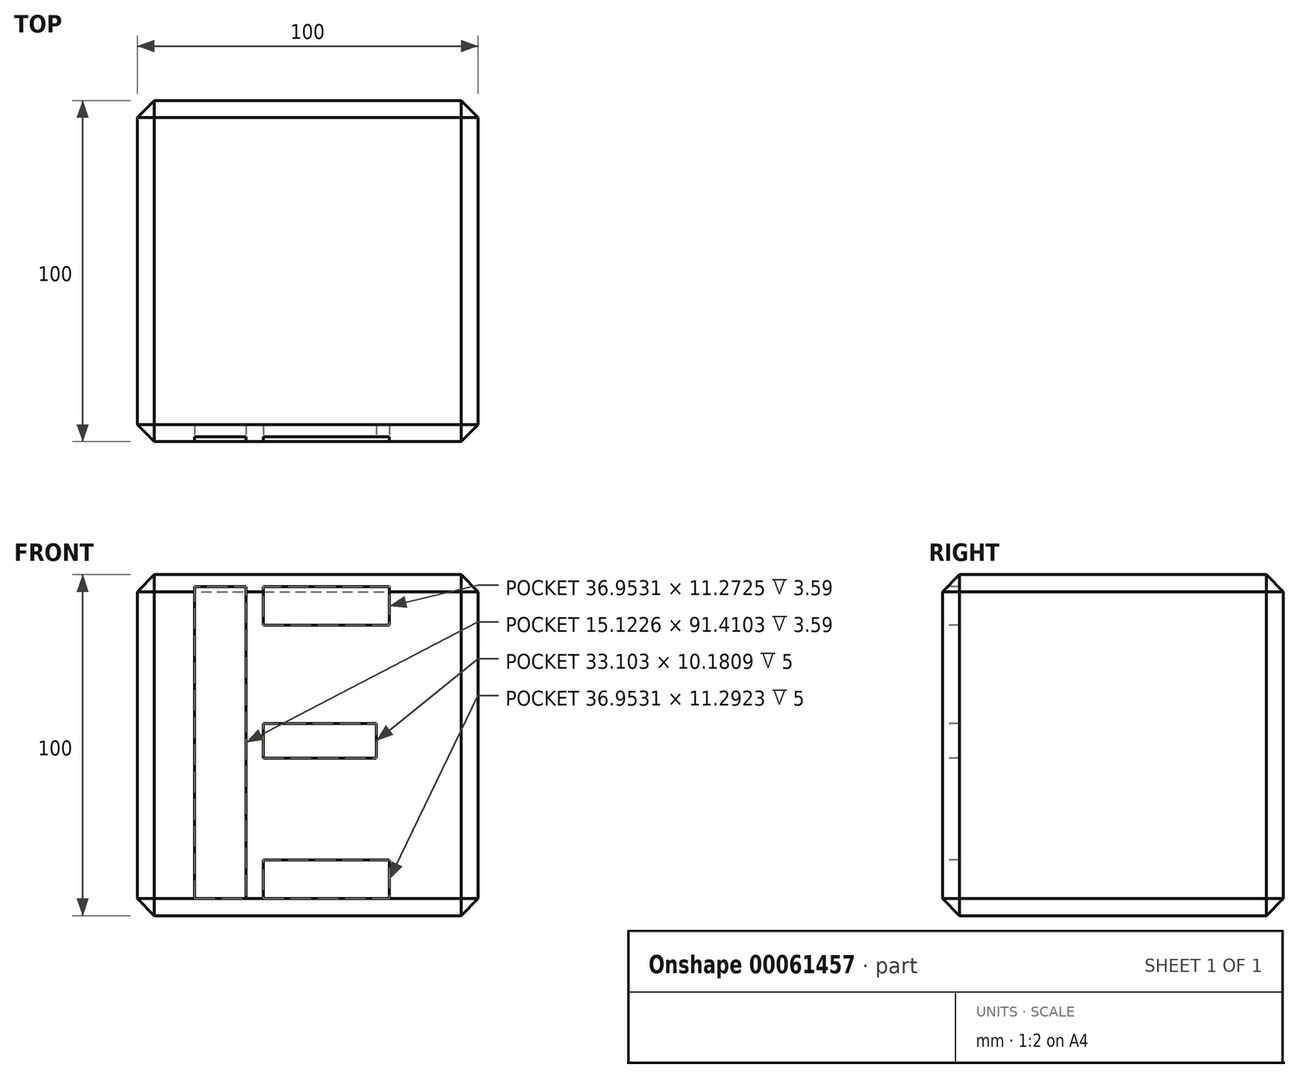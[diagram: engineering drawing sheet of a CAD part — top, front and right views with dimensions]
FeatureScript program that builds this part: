
annotation { "Feature Type Name" : "Feature", "Feature Type Description" : "" }
export const myFeature = defineFeature(function(context is Context, id is Id, definition is map)
    precondition{}
    {
        {
            var Q0;
            Q0=qCreatedBy(makeId("Front.planeOp"),FACE);
            var sketch = newSketch(context, id + "F0", { "sketchPlane" : qUnion([Q0])});
            skLineSegment(sketch, "E0.rect.bottom", {"start": v(50, -50) * mm, "end": v(-50, -50) * mm});
            skLineSegment(sketch, "E0.rect.top", {"start": v(50, 50) * mm, "end": v(-50, 50) * mm});
            skLineSegment(sketch, "E0.rect.left", {"start": v(50, -50) * mm, "end": v(50, 50) * mm});
            skLineSegment(sketch, "E0.rect.right", {"start": v(-50, -50) * mm, "end": v(-50, 50) * mm});
            skPoint(sketch, "E0.rect.middle", {"position": v(0, 0) * mm});
            skSolve(sketch);
        }
        {
            var Q0;
            Q0 = qSketchRegion(id + "F0", true);
            extrude(context, id + "F1", {"entities" : qUnion([Q0]), "endBound" : BoundingType.SYMMETRIC, "depth" : 100 * mm});
        }
        {
            var Q0;
            Q0=makeQuery(id+"F1.opExtrude","CAP_EDGE",EDGE,{"disambiguationData":[OSD([sQuery(id+"F0.wireOp",EDGE,"E0.rect.top")])],"isStart":false});
            var Q1;
            Q1=makeQuery(id+"F1.opExtrude","SWEPT_EDGE",EDGE,{"disambiguationData":[OSD([sQuery(id+"F0.wireOp",EDGE,"E0.rect.top"),sQuery(id+"F0.wireOp",EDGE,"E0.rect.right")])]});
            var Q2;
            Q2=makeQuery(id+"F1.opExtrude","CAP_EDGE",EDGE,{"disambiguationData":[OSD([sQuery(id+"F0.wireOp",EDGE,"E0.rect.top")])],"isStart":true});
            var Q3;
            Q3=makeQuery(id+"F1.opExtrude","SWEPT_EDGE",EDGE,{"disambiguationData":[OSD([sQuery(id+"F0.wireOp",EDGE,"E0.rect.top"),sQuery(id+"F0.wireOp",EDGE,"E0.rect.left")])]});
            var Q4;
            Q4=makeQuery(id+"F1.opExtrude","CAP_EDGE",EDGE,{"disambiguationData":[OSD([sQuery(id+"F0.wireOp",EDGE,"E0.rect.left")])],"isStart":false});
            var Q5;
            Q5=makeQuery(id+"F1.opExtrude","CAP_EDGE",EDGE,{"disambiguationData":[OSD([sQuery(id+"F0.wireOp",EDGE,"E0.rect.right")])],"isStart":false});
            var Q6;
            Q6=makeQuery(id+"F1.opExtrude","CAP_EDGE",EDGE,{"disambiguationData":[OSD([sQuery(id+"F0.wireOp",EDGE,"E0.rect.left")])],"isStart":true});
            var Q7;
            Q7=makeQuery(id+"F1.opExtrude","CAP_EDGE",EDGE,{"disambiguationData":[OSD([sQuery(id+"F0.wireOp",EDGE,"E0.rect.right")])],"isStart":true});
            var Q8;
            Q8=makeQuery(id+"F1.opExtrude","CAP_EDGE",EDGE,{"disambiguationData":[OSD([sQuery(id+"F0.wireOp",EDGE,"E0.rect.bottom")])],"isStart":true});
            var Q9;
            Q9=makeQuery(id+"F1.opExtrude","SWEPT_EDGE",EDGE,{"disambiguationData":[OSD([sQuery(id+"F0.wireOp",EDGE,"E0.rect.bottom"),sQuery(id+"F0.wireOp",EDGE,"E0.rect.right")])]});
            var Q10;
            Q10=makeQuery(id+"F1.opExtrude","SWEPT_EDGE",EDGE,{"disambiguationData":[OSD([sQuery(id+"F0.wireOp",EDGE,"E0.rect.bottom"),sQuery(id+"F0.wireOp",EDGE,"E0.rect.left")])]});
            var Q11;
            Q11=makeQuery(id+"F1.opExtrude","CAP_EDGE",EDGE,{"disambiguationData":[OSD([sQuery(id+"F0.wireOp",EDGE,"E0.rect.bottom")])],"isStart":false});
            chamfer(context, id + "F2", {"entities" : qUnion([Q0, Q1, Q2, Q3, Q4, Q5, Q6, Q7, Q8, Q9, Q10, Q11]), "width" : 5 * mm, "tangentPropagation" : true});
        }
        {
            var Q0;
            Q0=makeQuery(id+"F1.opExtrude","CAP_FACE",FACE,{"disambiguationData":[OSD([sQuery(id+"F0.wireOp",EDGE,"E0.rect.bottom"),sQuery(id+"F0.wireOp",EDGE,"E0.rect.top"),sQuery(id+"F0.wireOp",EDGE,"E0.rect.left"),sQuery(id+"F0.wireOp",EDGE,"E0.rect.right")])],"isStart":false});
            var sketch = newSketch(context, id + "F3", { "sketchPlane" : qUnion([Q0])});
            skText(sketch, "E1", { "text": "E", "fontName": "AllertaStencil-Regular.ttf"});
            const initialGuessF3  = {"E1": [-0.045, -0.045, 1, 0, 0.09145]};
            skSetInitialGuess(sketch, initialGuessF3);
            skSolve(sketch);
        }
        {
            var Q0;
            Q0 = qSketchRegion(id + "F3", true);
            extrude(context, id + "F4", {"entities" : qUnion([Q0]), "operationType" : NewBodyOperationType.REMOVE, "oppositeDirection" : true, "depth" : 5 * mm});
        }
    });
